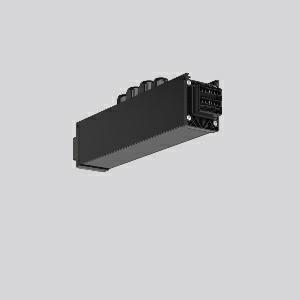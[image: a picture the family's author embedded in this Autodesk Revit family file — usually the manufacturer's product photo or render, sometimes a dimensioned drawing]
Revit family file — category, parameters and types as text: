
# Revit family: linedo_mitteleinspeisung_14pol_982698_003_710e
name_source: partatom
category: Lighting Fixtures
units: mm (PartAtom-declared; Revit-internal decimal feet)

## family parameters
Cut with Voids When Loaded = No
Host = Face
Light Source = No
Part Type = Normal
Room Calculation Point = No
Round Connector Dimension = Use Diameter
Shared = No

## types (1)
- LINEDO_Mitteleinspeisung_14pol
    Apparent Load = 0 VA
    Default Elevation = 1800 mm
    Description = Series: LINEDO
Middle power feed, 14-pole, connection socket / plug. Housing: extruded aluminium profile, powder-coated. Cover made of plastic, surface like housing. LINEDO plug system, plastic, black. 4 cable glands (2 x M20 and 2 x M25). Cable glands on top. Easy connection for rigid or flexible wires.
Colour: black
Length: 330 mm
Width: 58 mm
Height: 76 mm
Weight: 850 g
    Height = 76 mm
    Lamp = 0 x
    Length = 330 mm
    Luminous efficacy = 0 lm/W
    Manufacturer = RZB
    ModVariant = No
    Model = 982698.003
    Mounting Place = Ceiling
    Mounting Type = Surface mounted, Pendant
    Number of Poles = 1
    OnlyDefault = Yes
    Power Factor = 1
    Product Name = LINEDO_Mitteleinspeisung_14pol
    Product group = Surface mounted continuous line luminaire system
    ProductGroupID = 310
    Protection Class = Protection class I
    Protection Degree = IP 54
    RLX_Detail_Level = 1
    RLX_Emergency_Light_Flux = 0 lm
    RLX_Emergency_Type = 0
    RLX_Emergency_Type_DB = No
    RlxData = <blob elided: 23485 chars, md5=eaca6814>
    Standby Power = 0 W
    System Light Flux = 0 lm
    System Power = 0 W
    Type Comments = Product without accessories
    Type Image = 982698.003.2.jpg
    URL = http://relux.com
    VarID = ---
    Voltage = 0 V
    Weight = 0.00 kg
    Width = 58 mm

## geometry (parser evidence)
native form markers: Blend x4, Sweep x12
no freeform markers — native parametric forms only
